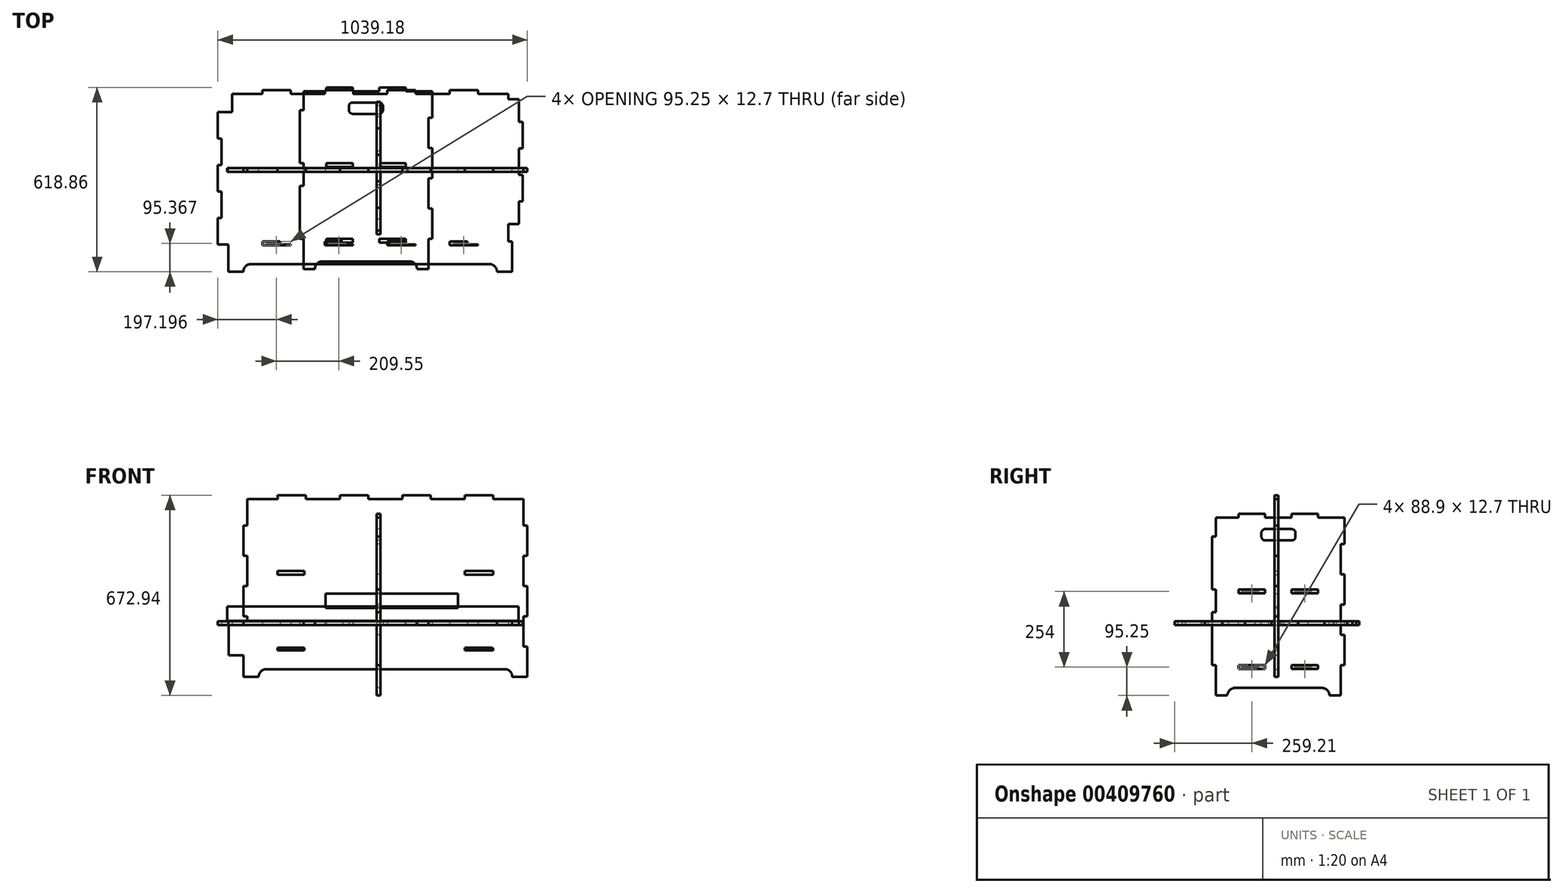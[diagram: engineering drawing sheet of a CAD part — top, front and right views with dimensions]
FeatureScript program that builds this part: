
annotation { "Feature Type Name" : "Feature", "Feature Type Description" : "" }
export const myFeature = defineFeature(function(context is Context, id is Id, definition is map)
    precondition{}
    {
        {
            var Q0;
            Q0=qCreatedBy(makeId("Top.planeOp"),FACE);
            var sketch = newSketch(context, id + "F0", { "sketchPlane" : qUnion([Q0])});
            skLineSegment(sketch, "E0.bottom", {"start": v(-520.7, -256.61) * mm, "end": v(-419.1, -256.61) * mm});
            skLineSegment(sketch, "E0.top", {"start": v(-520.7, 187.89) * mm, "end": v(-419.1, 187.89) * mm});
            skLineSegment(sketch, "E0.left", {"start": v(-520.7, -167.71) * mm, "end": v(-520.7, -78.8) * mm});
            skLineSegment(sketch, "E0.right", {"start": v(406.4, -167.71) * mm, "end": v(406.4, -79.99) * mm});
            skLineSegment(sketch, "E1.bottom", {"start": v(-533.4, 187.9) * mm, "end": v(-520.7, 187.9) * mm});
            skLineSegment(sketch, "E1.top", {"start": v(-533.4, 99) * mm, "end": v(-520.7, 99) * mm});
            skLineSegment(sketch, "E1.left", {"start": v(-533.4, 187.9) * mm, "end": v(-533.4, 99) * mm});
            skLineSegment(sketch, "E1.right", {"start": v(-520.7, 187.9) * mm, "end": v(-520.7, 187.89) * mm});
            skLineSegment(sketch, "E2.bottom", {"start": v(-520.7, -256.61) * mm, "end": v(-533.4, -256.61) * mm});
            skLineSegment(sketch, "E2.top", {"start": v(-520.7, -167.71) * mm, "end": v(-533.4, -167.71) * mm});
            skLineSegment(sketch, "E2.right", {"start": v(-533.4, -256.61) * mm, "end": v(-533.4, -167.71) * mm});
            skLineSegment(sketch, "E3.bottom", {"start": v(-533.4, 10.1) * mm, "end": v(-520.7, 10.1) * mm});
            skLineSegment(sketch, "E3.top", {"start": v(-533.4, -78.8) * mm, "end": v(-520.7, -78.8) * mm});
            skLineSegment(sketch, "E3.left", {"start": v(-533.4, 10.1) * mm, "end": v(-533.4, -78.8) * mm});
            skLineSegment(sketch, "E4.top", {"start": v(406.4, 98.99) * mm, "end": v(419.1, 98.99) * mm});
            skLineSegment(sketch, "E5.top", {"start": v(406.4, -167.71) * mm, "end": v(419.1, -167.71) * mm});
            skLineSegment(sketch, "E6.bottom", {"start": v(406.4, 10.09) * mm, "end": v(419.1, 10.09) * mm});
            skLineSegment(sketch, "E6.top", {"start": v(406.4, -79.99) * mm, "end": v(419.1, -79.99) * mm});
            skLineSegment(sketch, "E6.right", {"start": v(419.1, 10.09) * mm, "end": v(419.1, -79.99) * mm});
            skLineSegment(sketch, "E7.top", {"start": v(-419.1, 175.19) * mm, "end": v(-323.85, 175.19) * mm});
            skLineSegment(sketch, "E7.left", {"start": v(-419.1, 187.89) * mm, "end": v(-419.1, 175.19) * mm});
            skLineSegment(sketch, "E7.right", {"start": v(-323.85, 187.89) * mm, "end": v(-323.85, 175.19) * mm});
            skLineSegment(sketch, "E8.trimOffspring", {"start": v(-323.85, 187.89) * mm, "end": v(-209.55, 187.89) * mm});
            skLineSegment(sketch, "E9.trimOffspring", {"start": v(-520.7, 10.1) * mm, "end": v(-520.7, 99) * mm});
            skLineSegment(sketch, "E10.trimOffspring", {"start": v(406.4, 10.09) * mm, "end": v(406.4, 98.99) * mm});
            skLineSegment(sketch, "E11.top", {"start": v(-209.55, 175.19) * mm, "end": v(-114.3, 175.19) * mm});
            skLineSegment(sketch, "E11.left", {"start": v(-209.55, 187.89) * mm, "end": v(-209.55, 175.19) * mm});
            skLineSegment(sketch, "E11.right", {"start": v(-114.3, 187.89) * mm, "end": v(-114.3, 175.19) * mm});
            skLineSegment(sketch, "E12.top", {"start": v(0, 175.19) * mm, "end": v(95.25, 175.19) * mm});
            skLineSegment(sketch, "E12.left", {"start": v(0, 187.89) * mm, "end": v(0, 175.19) * mm});
            skLineSegment(sketch, "E12.right", {"start": v(95.25, 187.89) * mm, "end": v(95.25, 175.19) * mm});
            skLineSegment(sketch, "E13.top", {"start": v(209.55, 175.19) * mm, "end": v(304.8, 175.19) * mm});
            skLineSegment(sketch, "E13.left", {"start": v(209.55, 187.89) * mm, "end": v(209.55, 175.19) * mm});
            skLineSegment(sketch, "E13.right", {"start": v(304.8, 187.89) * mm, "end": v(304.8, 175.19) * mm});
            skLineSegment(sketch, "E14.trimOffspring", {"start": v(-114.3, 187.89) * mm, "end": v(0, 187.89) * mm});
            skLineSegment(sketch, "E15.trimOffspring", {"start": v(95.25, 187.89) * mm, "end": v(209.55, 187.89) * mm});
            skLineSegment(sketch, "E16.top", {"start": v(-419.1, -243.91) * mm, "end": v(-323.85, -243.91) * mm});
            skLineSegment(sketch, "E16.left", {"start": v(-419.1, -256.61) * mm, "end": v(-419.1, -243.91) * mm});
            skLineSegment(sketch, "E16.right", {"start": v(-323.85, -256.61) * mm, "end": v(-323.85, -243.91) * mm});
            skLineSegment(sketch, "E17.top", {"start": v(-209.55, -243.91) * mm, "end": v(-114.3, -243.91) * mm});
            skLineSegment(sketch, "E17.left", {"start": v(-209.55, -256.61) * mm, "end": v(-209.55, -243.91) * mm});
            skLineSegment(sketch, "E17.right", {"start": v(-114.3, -256.61) * mm, "end": v(-114.3, -243.91) * mm});
            skLineSegment(sketch, "E18.top", {"start": v(0, -243.91) * mm, "end": v(95.25, -243.91) * mm});
            skLineSegment(sketch, "E18.left", {"start": v(0, -256.61) * mm, "end": v(0, -243.91) * mm});
            skLineSegment(sketch, "E18.right", {"start": v(95.25, -256.61) * mm, "end": v(95.25, -243.91) * mm});
            skLineSegment(sketch, "E19.top", {"start": v(209.55, -243.91) * mm, "end": v(304.8, -243.91) * mm});
            skLineSegment(sketch, "E19.left", {"start": v(209.55, -256.61) * mm, "end": v(209.55, -243.91) * mm});
            skLineSegment(sketch, "E19.right", {"start": v(304.8, -256.61) * mm, "end": v(304.8, -243.91) * mm});
            skLineSegment(sketch, "E20.trimOffspring", {"start": v(-323.85, -256.61) * mm, "end": v(-209.55, -256.61) * mm});
            skLineSegment(sketch, "E21.trimOffspring", {"start": v(-114.3, -256.61) * mm, "end": v(0, -256.61) * mm});
            skLineSegment(sketch, "E22.trimOffspring", {"start": v(95.25, -256.61) * mm, "end": v(209.55, -256.61) * mm});
            skLineSegment(sketch, "E23.trimOffspring", {"start": v(304.8, -256.61) * mm, "end": v(406.4, -256.61) * mm});
            skPoint(sketch, "E24.right.end.orphan", {"position": v(419.1, 175.19) * mm});
            skPoint(sketch, "E4.right.start.orphan", {"position": v(433.58, 187.89) * mm});
            skLineSegment(sketch, "E25", {"start": v(419.1, 98.99) * mm, "end": v(419.1, 187.89) * mm});
            skPoint(sketch, "E4.bottom.start.orphan", {"position": v(406.4, 187.89) * mm});
            skLineSegment(sketch, "E26", {"start": v(304.8, 187.89) * mm, "end": v(419.1, 187.89) * mm});
            skLineSegment(sketch, "E27", {"start": v(419.1, -167.71) * mm, "end": v(419.1, -256.61) * mm});
            skLineSegment(sketch, "E28", {"start": v(419.1, -256.61) * mm, "end": v(406.4, -256.61) * mm});
            skSolve(sketch);
        }
        {
            var Q0;
            Q0 = qSketchRegion(id + "F0", true);
            extrude(context, id + "F1", {"entities" : qUnion([Q0]), "depth" : 12.7 * mm});
        }
        {
            var Q0;
            Q0=qCreatedBy(makeId("Top.planeOp"),FACE);
            var sketch = newSketch(context, id + "F2", { "sketchPlane" : qUnion([Q0])});
            skLineSegment(sketch, "E29.bottom", {"start": v(-347.77, 244.35) * mm, "end": v(-252.52, 244.35) * mm});
            skLineSegment(sketch, "E29.top", {"start": v(-347.77, -200.15) * mm, "end": v(-252.52, -200.15) * mm});
            skLineSegment(sketch, "E29.left", {"start": v(-449.37, 231.65) * mm, "end": v(-449.37, 155.45) * mm});
            skLineSegment(sketch, "E29.right", {"start": v(477.73, 231.65) * mm, "end": v(477.73, 155.45) * mm});
            skLineSegment(sketch, "E30.bottom", {"start": v(-449.37, 155.45) * mm, "end": v(-462.07, 155.45) * mm});
            skLineSegment(sketch, "E30.top", {"start": v(-449.37, 66.55) * mm, "end": v(-462.07, 66.55) * mm});
            skLineSegment(sketch, "E30.right", {"start": v(-462.07, 155.45) * mm, "end": v(-462.07, 66.55) * mm});
            skLineSegment(sketch, "E31.bottom", {"start": v(-449.37, -22.35) * mm, "end": v(-462.07, -22.35) * mm});
            skLineSegment(sketch, "E31.top", {"start": v(-449.37, -111.25) * mm, "end": v(-462.07, -111.25) * mm});
            skLineSegment(sketch, "E31.right", {"start": v(-462.07, -22.35) * mm, "end": v(-462.07, -111.25) * mm});
            skLineSegment(sketch, "E32.trimOffspring", {"start": v(-449.37, 66.55) * mm, "end": v(-449.37, -22.35) * mm});
            skLineSegment(sketch, "E33.trimOffspring", {"start": v(-449.37, -111.25) * mm, "end": v(-449.37, -187.45) * mm});
            skLineSegment(sketch, "E34.bottom", {"start": v(477.73, 155.45) * mm, "end": v(490.43, 155.45) * mm});
            skLineSegment(sketch, "E34.top", {"start": v(477.73, 66.55) * mm, "end": v(490.43, 66.55) * mm});
            skLineSegment(sketch, "E34.right", {"start": v(490.43, 155.45) * mm, "end": v(490.43, 66.55) * mm});
            skLineSegment(sketch, "E35.bottom", {"start": v(477.73, -22.35) * mm, "end": v(490.43, -22.35) * mm});
            skLineSegment(sketch, "E35.top", {"start": v(477.73, -111.25) * mm, "end": v(490.43, -111.25) * mm});
            skLineSegment(sketch, "E35.right", {"start": v(490.43, -22.35) * mm, "end": v(490.43, -111.25) * mm});
            skLineSegment(sketch, "E36.trimOffspring", {"start": v(477.73, 66.55) * mm, "end": v(477.73, -22.35) * mm});
            skLineSegment(sketch, "E37.trimOffspring", {"start": v(477.73, -111.25) * mm, "end": v(477.73, -187.45) * mm});
            skLineSegment(sketch, "E38.top", {"start": v(-449.37, 231.65) * mm, "end": v(-347.77, 231.65) * mm});
            skLineSegment(sketch, "E38.right", {"start": v(-347.77, 244.35) * mm, "end": v(-347.77, 231.65) * mm});
            skLineSegment(sketch, "E39.top", {"start": v(-252.52, 231.65) * mm, "end": v(-138.22, 231.65) * mm});
            skLineSegment(sketch, "E39.left", {"start": v(-252.52, 244.35) * mm, "end": v(-252.52, 231.65) * mm});
            skLineSegment(sketch, "E39.right", {"start": v(-138.22, 244.35) * mm, "end": v(-138.22, 231.65) * mm});
            skPoint(sketch, "E38.left.start.orphan", {"position": v(-449.37, 244.35) * mm});
            skPoint(sketch, "E40.trimOffspring.end.orphan", {"position": v(14.18, 244.35) * mm});
            skLineSegment(sketch, "E41", {"start": v(-138.22, 244.35) * mm, "end": v(-42.97, 244.35) * mm});
            skLineSegment(sketch, "E42.top", {"start": v(-42.97, 231.65) * mm, "end": v(71.33, 231.65) * mm});
            skLineSegment(sketch, "E42.left", {"start": v(-42.97, 244.35) * mm, "end": v(-42.97, 231.65) * mm});
            skLineSegment(sketch, "E42.right", {"start": v(71.33, 244.35) * mm, "end": v(71.33, 231.65) * mm});
            skLineSegment(sketch, "E43.trimOffspring", {"start": v(71.33, 244.35) * mm, "end": v(166.58, 244.35) * mm});
            skLineSegment(sketch, "E44.top", {"start": v(166.58, 231.65) * mm, "end": v(280.88, 231.65) * mm});
            skLineSegment(sketch, "E44.left", {"start": v(166.58, 244.35) * mm, "end": v(166.58, 231.65) * mm});
            skLineSegment(sketch, "E44.right", {"start": v(280.88, 244.35) * mm, "end": v(280.88, 231.65) * mm});
            skLineSegment(sketch, "E45.trimOffspring", {"start": v(280.88, 244.35) * mm, "end": v(376.13, 244.35) * mm});
            skLineSegment(sketch, "E46.top", {"start": v(477.73, 231.65) * mm, "end": v(376.13, 231.65) * mm});
            skLineSegment(sketch, "E46.right", {"start": v(376.13, 244.35) * mm, "end": v(376.13, 231.65) * mm});
            skPoint(sketch, "E47.orphan", {"position": v(477.73, 244.35) * mm});
            skLineSegment(sketch, "E48.top", {"start": v(-347.77, -187.45) * mm, "end": v(-449.37, -187.45) * mm});
            skLineSegment(sketch, "E48.left", {"start": v(-347.77, -200.15) * mm, "end": v(-347.77, -187.45) * mm});
            skLineSegment(sketch, "E49.top", {"start": v(-252.52, -187.45) * mm, "end": v(-138.22, -187.45) * mm});
            skLineSegment(sketch, "E49.left", {"start": v(-252.52, -200.15) * mm, "end": v(-252.52, -187.45) * mm});
            skLineSegment(sketch, "E49.right", {"start": v(-138.22, -200.15) * mm, "end": v(-138.22, -187.45) * mm});
            skLineSegment(sketch, "E50.top", {"start": v(-42.97, -187.45) * mm, "end": v(71.33, -187.45) * mm});
            skLineSegment(sketch, "E50.left", {"start": v(-42.97, -200.15) * mm, "end": v(-42.97, -187.45) * mm});
            skLineSegment(sketch, "E50.right", {"start": v(71.33, -200.15) * mm, "end": v(71.33, -187.45) * mm});
            skLineSegment(sketch, "E51.top", {"start": v(166.58, -187.45) * mm, "end": v(280.88, -187.45) * mm});
            skLineSegment(sketch, "E51.left", {"start": v(166.58, -200.15) * mm, "end": v(166.58, -187.45) * mm});
            skLineSegment(sketch, "E51.right", {"start": v(280.88, -200.15) * mm, "end": v(280.88, -187.45) * mm});
            skLineSegment(sketch, "E52.top", {"start": v(376.13, -187.45) * mm, "end": v(477.73, -187.45) * mm});
            skLineSegment(sketch, "E52.left", {"start": v(376.13, -200.15) * mm, "end": v(376.13, -187.45) * mm});
            skPoint(sketch, "E48.right.start.orphan", {"position": v(-449.37, -200.15) * mm});
            skLineSegment(sketch, "E53.trimOffspring", {"start": v(-138.22, -200.15) * mm, "end": v(-42.97, -200.15) * mm});
            skLineSegment(sketch, "E54.trimOffspring", {"start": v(71.33, -200.15) * mm, "end": v(166.58, -200.15) * mm});
            skLineSegment(sketch, "E55.trimOffspring", {"start": v(280.88, -200.15) * mm, "end": v(376.13, -200.15) * mm});
            skPoint(sketch, "E56.orphan", {"position": v(477.73, -200.15) * mm});
            skSolve(sketch);
        }
        {
            var Q0;
            Q0=makeQuery(id+"F2.imprint","IMPRINT",FACE,{"disambiguationData":[TD([[makeQuery(id+"F2.imprint","IMPRINT",EDGE,{"derivedFrom":sQuery(id+"F2.wireOp",EDGE,"E29.bottom")}),-1.0]])]});
            extrude(context, id + "F3", {"entities" : qUnion([Q0]), "depth" : 12.7 * mm});
        }
        {
            var Q0;
            Q0=qCreatedBy(makeId("Front.planeOp"),FACE);
            var sketch = newSketch(context, id + "F4", { "sketchPlane" : qUnion([Q0])});
            skLineSegment(sketch, "E57.bottom", {"start": v(-446.72, -173.54) * mm, "end": v(-395.92, -173.54) * mm});
            skLineSegment(sketch, "E57.top", {"start": v(-332.42, 436.06) * mm, "end": v(-237.17, 436.06) * mm});
            skLineSegment(sketch, "E57.left", {"start": v(-446.72, -173.54) * mm, "end": v(-446.72, -71.94) * mm});
            skLineSegment(sketch, "E57.right", {"start": v(505.78, -173.66) * mm, "end": v(505.78, -72.06) * mm});
            skLineSegment(sketch, "E58.top", {"start": v(-434.02, 423.36) * mm, "end": v(-331.85, 423.36) * mm});
            skLineSegment(sketch, "E58.right", {"start": v(-332.42, 436.06) * mm, "end": v(-331.85, 423.36) * mm});
            skLineSegment(sketch, "E59.top", {"start": v(-237.17, 423.24) * mm, "end": v(-122.87, 423.24) * mm});
            skLineSegment(sketch, "E59.left", {"start": v(-237.17, 436.06) * mm, "end": v(-237.17, 423.24) * mm});
            skLineSegment(sketch, "E59.right", {"start": v(-122.87, 436.06) * mm, "end": v(-122.87, 423.24) * mm});
            skLineSegment(sketch, "E60.top", {"start": v(-27.62, 423.24) * mm, "end": v(86.68, 423.24) * mm});
            skLineSegment(sketch, "E60.left", {"start": v(-27.62, 436.06) * mm, "end": v(-27.62, 423.24) * mm});
            skLineSegment(sketch, "E60.right", {"start": v(86.68, 436.06) * mm, "end": v(86.68, 423.24) * mm});
            skLineSegment(sketch, "E61.top", {"start": v(181.93, 423.24) * mm, "end": v(296.23, 423.24) * mm});
            skLineSegment(sketch, "E61.left", {"start": v(181.93, 436.06) * mm, "end": v(181.93, 423.24) * mm});
            skLineSegment(sketch, "E61.right", {"start": v(296.23, 436.06) * mm, "end": v(296.23, 423.24) * mm});
            skLineSegment(sketch, "E62.top", {"start": v(391.48, 423.36) * mm, "end": v(493.08, 423.36) * mm});
            skLineSegment(sketch, "E62.left", {"start": v(391.48, 436.06) * mm, "end": v(391.48, 423.36) * mm});
            skLineSegment(sketch, "E63.trimOffspring", {"start": v(-122.87, 436.06) * mm, "end": v(-27.62, 436.06) * mm});
            skLineSegment(sketch, "E64.trimOffspring", {"start": v(86.68, 436.06) * mm, "end": v(181.93, 436.06) * mm});
            skLineSegment(sketch, "E65.trimOffspring", {"start": v(296.23, 436.06) * mm, "end": v(391.48, 436.06) * mm});
            skLineSegment(sketch, "E66.top", {"start": v(-370.52, -148.14) * mm, "end": v(429.58, -148.14) * mm});
            skLineSegment(sketch, "E66.left", {"start": v(-395.92, -173.54) * mm, "end": v(-395.92, -173.54) * mm});
            skPoint(sketch, "E67.visualSharp", {"position": v(-395.92, -148.14) * mm});
            skArc(sketch, "E67.filletArc", {"start": v(-370.52, -148.14) * mm, "mid": v(-388.48, -155.58) * mm, "end": v(-395.92, -173.54) * mm});
            skPoint(sketch, "E68.visualSharp", {"position": v(454.98, -148.14) * mm});
            skArc(sketch, "E68.filletArc", {"start": v(454.98, -173.66) * mm, "mid": v(447.58, -155.62) * mm, "end": v(429.58, -148.14) * mm});
            skLineSegment(sketch, "E69.trimOffspring", {"start": v(454.98, -173.66) * mm, "end": v(505.78, -173.66) * mm});
            skLineSegment(sketch, "E70.top", {"start": v(505.78, 334.34) * mm, "end": v(493.08, 334.34) * mm});
            skLineSegment(sketch, "E70.right", {"start": v(493.08, 423.36) * mm, "end": v(493.08, 334.34) * mm});
            skLineSegment(sketch, "E71.bottom", {"start": v(505.78, 232.74) * mm, "end": v(493.08, 232.74) * mm});
            skLineSegment(sketch, "E71.top", {"start": v(505.78, 131.14) * mm, "end": v(493.08, 131.14) * mm});
            skLineSegment(sketch, "E71.right", {"start": v(493.08, 232.74) * mm, "end": v(493.08, 131.14) * mm});
            skLineSegment(sketch, "E72.bottom", {"start": v(505.78, 29.54) * mm, "end": v(493.08, 29.54) * mm});
            skLineSegment(sketch, "E72.top", {"start": v(505.78, -72.06) * mm, "end": v(493.08, -72.06) * mm});
            skLineSegment(sketch, "E72.right", {"start": v(493.08, 29.54) * mm, "end": v(493.08, -72.06) * mm});
            skLineSegment(sketch, "E73.top", {"start": v(-446.72, 334.46) * mm, "end": v(-434.02, 334.46) * mm});
            skLineSegment(sketch, "E73.right", {"start": v(-434.02, 423.36) * mm, "end": v(-434.02, 334.46) * mm});
            skPoint(sketch, "E74.oppositeSnap0", {"position": v(-446.72, 131.26) * mm});
            skLineSegment(sketch, "E74.bottom", {"start": v(-446.72, 232.86) * mm, "end": v(-434.02, 232.86) * mm});
            skLineSegment(sketch, "E74.top", {"start": v(-446.72, 131.26) * mm, "end": v(-434.02, 131.26) * mm});
            skLineSegment(sketch, "E74.right", {"start": v(-434.02, 232.86) * mm, "end": v(-434.02, 131.26) * mm});
            skLineSegment(sketch, "E75.bottom", {"start": v(-446.72, 29.66) * mm, "end": v(-434.02, 29.66) * mm});
            skLineSegment(sketch, "E75.top", {"start": v(-446.72, -71.94) * mm, "end": v(-434.02, -71.94) * mm});
            skLineSegment(sketch, "E75.right", {"start": v(-434.02, 29.66) * mm, "end": v(-434.02, -71.94) * mm});
            skPoint(sketch, "E76.trimOffspring.start.orphan", {"position": v(493.08, 435.94) * mm});
            skPoint(sketch, "E62.right.start.orphan", {"position": v(505.78, 435.94) * mm});
            skLineSegment(sketch, "E77.trimOffspring", {"start": v(505.78, 232.74) * mm, "end": v(505.78, 334.34) * mm});
            skLineSegment(sketch, "E78.trimOffspring", {"start": v(505.78, 29.54) * mm, "end": v(505.78, 131.14) * mm});
            skLineSegment(sketch, "E79.trimOffspring", {"start": v(-446.72, 232.86) * mm, "end": v(-446.72, 334.46) * mm});
            skLineSegment(sketch, "E80.trimOffspring", {"start": v(-446.72, 29.66) * mm, "end": v(-446.72, 131.26) * mm});
            skPoint(sketch, "E81.orphan", {"position": v(-446.72, 436.06) * mm});
            skPoint(sketch, "E82.orphan", {"position": v(-434.02, 436.06) * mm});
            skPoint(sketch, "E83.orphan", {"position": v(-446.72, 423.36) * mm});
            skLineSegment(sketch, "E84.bottom", {"start": v(-332.42, 182.06) * mm, "end": v(-237.17, 182.06) * mm});
            skLineSegment(sketch, "E84.top", {"start": v(-332.42, 169.36) * mm, "end": v(-237.17, 169.36) * mm});
            skLineSegment(sketch, "E84.left", {"start": v(-332.42, 182.06) * mm, "end": v(-332.42, 169.36) * mm});
            skLineSegment(sketch, "E84.right", {"start": v(-237.17, 182.06) * mm, "end": v(-237.17, 169.36) * mm});
            skLineSegment(sketch, "E85.bottom", {"start": v(-122.87, 182.06) * mm, "end": v(-27.62, 182.06) * mm});
            skLineSegment(sketch, "E85.top", {"start": v(-122.87, 169.74) * mm, "end": v(-27.62, 169.74) * mm});
            skLineSegment(sketch, "E85.left", {"start": v(-122.87, 182.06) * mm, "end": v(-122.87, 169.74) * mm});
            skLineSegment(sketch, "E85.right", {"start": v(-27.62, 182.06) * mm, "end": v(-27.62, 169.74) * mm});
            skLineSegment(sketch, "E86.bottom", {"start": v(86.68, 182.06) * mm, "end": v(181.93, 182.06) * mm});
            skLineSegment(sketch, "E86.top", {"start": v(86.68, 169.36) * mm, "end": v(181.93, 169.36) * mm});
            skLineSegment(sketch, "E86.left", {"start": v(86.68, 182.06) * mm, "end": v(86.68, 169.36) * mm});
            skLineSegment(sketch, "E86.right", {"start": v(181.93, 182.06) * mm, "end": v(181.93, 169.36) * mm});
            skLineSegment(sketch, "E87.bottom", {"start": v(296.23, 182.06) * mm, "end": v(391.48, 182.06) * mm});
            skLineSegment(sketch, "E87.top", {"start": v(296.23, 169.36) * mm, "end": v(391.48, 169.36) * mm});
            skLineSegment(sketch, "E87.left", {"start": v(296.23, 182.06) * mm, "end": v(296.23, 169.36) * mm});
            skLineSegment(sketch, "E87.right", {"start": v(391.48, 182.06) * mm, "end": v(391.48, 169.36) * mm});
            skLineSegment(sketch, "E88.bottom", {"start": v(-332.42, -71.94) * mm, "end": v(-237.17, -71.94) * mm});
            skLineSegment(sketch, "E88.top", {"start": v(-332.42, -84.64) * mm, "end": v(-237.17, -84.64) * mm});
            skLineSegment(sketch, "E88.left", {"start": v(-332.42, -71.94) * mm, "end": v(-332.42, -84.64) * mm});
            skLineSegment(sketch, "E88.right", {"start": v(-237.17, -71.94) * mm, "end": v(-237.17, -84.64) * mm});
            skLineSegment(sketch, "E89.bottom", {"start": v(-122.87, -71.94) * mm, "end": v(-27.62, -71.94) * mm});
            skLineSegment(sketch, "E89.top", {"start": v(-122.87, -84.64) * mm, "end": v(-27.62, -84.64) * mm});
            skLineSegment(sketch, "E89.left", {"start": v(-122.87, -71.94) * mm, "end": v(-122.87, -84.64) * mm});
            skLineSegment(sketch, "E89.right", {"start": v(-27.62, -71.94) * mm, "end": v(-27.62, -84.64) * mm});
            skPoint(sketch, "E90.oppositeSnap0", {"position": v(-75.24, -84.64) * mm});
            skLineSegment(sketch, "E90.bottom", {"start": v(86.68, -71.94) * mm, "end": v(181.93, -71.94) * mm});
            skLineSegment(sketch, "E90.top", {"start": v(86.68, -84.64) * mm, "end": v(181.93, -84.64) * mm});
            skLineSegment(sketch, "E90.left", {"start": v(86.68, -71.94) * mm, "end": v(86.68, -84.64) * mm});
            skLineSegment(sketch, "E90.right", {"start": v(181.93, -71.94) * mm, "end": v(181.93, -84.64) * mm});
            skLineSegment(sketch, "E91.bottom", {"start": v(296.23, -71.94) * mm, "end": v(391.48, -71.94) * mm});
            skLineSegment(sketch, "E91.top", {"start": v(296.23, -84.64) * mm, "end": v(391.48, -84.64) * mm});
            skLineSegment(sketch, "E91.left", {"start": v(296.23, -71.94) * mm, "end": v(296.23, -84.64) * mm});
            skLineSegment(sketch, "E91.right", {"start": v(391.48, -71.94) * mm, "end": v(391.48, -84.64) * mm});
            skPoint(sketch, "E66.right.start.orphan", {"position": v(454.98, -160.96) * mm});
            skSolve(sketch);
        }
        {
            var Q0;
            Q0 = qSketchRegion(id + "F4", true);
            extrude(context, id + "F5", {"entities" : qUnion([Q0]), "depth" : 12.7 * mm});
        }
        {
            var Q0;
            Q0=qCreatedBy(makeId("Right.planeOp"),FACE);
            var sketch = newSketch(context, id + "F6", { "sketchPlane" : qUnion([Q0])});
            skLineSegment(sketch, "E92.bottom", {"start": v(-132.95, 372.72) * mm, "end": v(-44.05, 372.72) * mm});
            skLineSegment(sketch, "E92.top", {"start": v(-209.15, -236.88) * mm, "end": v(-171.05, -236.88) * mm});
            skLineSegment(sketch, "E92.left", {"start": v(-221.85, 296.52) * mm, "end": v(-221.85, 118.72) * mm});
            skLineSegment(sketch, "E93.top", {"start": v(-145.65, -211.48) * mm, "end": v(146.45, -211.48) * mm});
            skLineSegment(sketch, "E93.left", {"start": v(-171.05, -236.88) * mm, "end": v(-171.05, -236.88) * mm});
            skLineSegment(sketch, "E93.right", {"start": v(171.85, -236.88) * mm, "end": v(171.85, -236.88) * mm});
            skLineSegment(sketch, "E94.trimOffspring", {"start": v(171.85, -236.88) * mm, "end": v(209.95, -236.88) * mm});
            skPoint(sketch, "E95.visualSharp", {"position": v(-171.05, -211.48) * mm});
            skArc(sketch, "E95.filletArc", {"start": v(-145.65, -211.48) * mm, "mid": v(-163.61, -218.92) * mm, "end": v(-171.05, -236.88) * mm});
            skPoint(sketch, "E96.visualSharp", {"position": v(171.85, -211.48) * mm});
            skArc(sketch, "E96.filletArc", {"start": v(171.85, -236.88) * mm, "mid": v(164.41, -218.92) * mm, "end": v(146.45, -211.48) * mm});
            skLineSegment(sketch, "E97.top", {"start": v(-209.15, 360.02) * mm, "end": v(-132.95, 360.02) * mm});
            skLineSegment(sketch, "E97.right", {"start": v(-132.95, 372.72) * mm, "end": v(-132.95, 360.02) * mm});
            skLineSegment(sketch, "E98.top", {"start": v(-44.05, 360.02) * mm, "end": v(44.85, 360.02) * mm});
            skLineSegment(sketch, "E98.left", {"start": v(-44.05, 372.72) * mm, "end": v(-44.05, 360.02) * mm});
            skLineSegment(sketch, "E98.right", {"start": v(44.85, 372.72) * mm, "end": v(44.85, 360.02) * mm});
            skLineSegment(sketch, "E99.top", {"start": v(209.95, 360.02) * mm, "end": v(133.75, 360.02) * mm});
            skLineSegment(sketch, "E99.right", {"start": v(133.75, 372.72) * mm, "end": v(133.75, 360.02) * mm});
            skLineSegment(sketch, "E100.top", {"start": v(222.65, 271.12) * mm, "end": v(209.95, 271.12) * mm});
            skLineSegment(sketch, "E101.bottom", {"start": v(222.65, 169.52) * mm, "end": v(209.95, 169.52) * mm});
            skLineSegment(sketch, "E101.top", {"start": v(222.65, 67.92) * mm, "end": v(209.95, 67.92) * mm});
            skLineSegment(sketch, "E102.bottom", {"start": v(222.65, -33.68) * mm, "end": v(209.95, -33.68) * mm});
            skLineSegment(sketch, "E102.top", {"start": v(222.65, -135.28) * mm, "end": v(209.95, -135.28) * mm});
            skLineSegment(sketch, "E103.bottom", {"start": v(-132.95, 118.72) * mm, "end": v(-44.05, 118.72) * mm});
            skLineSegment(sketch, "E103.top", {"start": v(-132.95, 106.02) * mm, "end": v(-44.05, 106.02) * mm});
            skLineSegment(sketch, "E103.left", {"start": v(-132.95, 118.72) * mm, "end": v(-132.95, 106.02) * mm});
            skLineSegment(sketch, "E103.right", {"start": v(-44.05, 118.72) * mm, "end": v(-44.05, 106.02) * mm});
            skLineSegment(sketch, "E104.bottom", {"start": v(44.85, 118.72) * mm, "end": v(133.75, 118.72) * mm});
            skLineSegment(sketch, "E104.top", {"start": v(44.85, 106.02) * mm, "end": v(133.75, 106.02) * mm});
            skLineSegment(sketch, "E104.left", {"start": v(44.85, 118.72) * mm, "end": v(44.85, 106.02) * mm});
            skLineSegment(sketch, "E104.right", {"start": v(133.75, 118.72) * mm, "end": v(133.75, 106.02) * mm});
            skLineSegment(sketch, "E105.bottom", {"start": v(-132.95, -135.28) * mm, "end": v(-44.05, -135.28) * mm});
            skLineSegment(sketch, "E105.top", {"start": v(-132.95, -147.98) * mm, "end": v(-44.05, -147.98) * mm});
            skLineSegment(sketch, "E105.left", {"start": v(-132.95, -135.28) * mm, "end": v(-132.95, -147.98) * mm});
            skLineSegment(sketch, "E105.right", {"start": v(-44.05, -135.28) * mm, "end": v(-44.05, -147.98) * mm});
            skLineSegment(sketch, "E106.bottom", {"start": v(44.85, -135.28) * mm, "end": v(133.75, -135.28) * mm});
            skLineSegment(sketch, "E106.top", {"start": v(44.85, -147.98) * mm, "end": v(133.75, -147.98) * mm});
            skLineSegment(sketch, "E106.left", {"start": v(44.85, -135.28) * mm, "end": v(44.85, -147.98) * mm});
            skLineSegment(sketch, "E106.right", {"start": v(133.75, -135.28) * mm, "end": v(133.75, -147.98) * mm});
            skLineSegment(sketch, "E107.bottom", {"start": v(-44.05, 321.92) * mm, "end": v(44.85, 321.92) * mm});
            skLineSegment(sketch, "E107.top", {"start": v(-44.05, 283.82) * mm, "end": v(44.85, 283.82) * mm});
            skLineSegment(sketch, "E107.left", {"start": v(-56.75, 309.22) * mm, "end": v(-56.75, 296.52) * mm});
            skLineSegment(sketch, "E107.right", {"start": v(57.55, 309.22) * mm, "end": v(57.55, 296.52) * mm});
            skLineSegment(sketch, "E108.top", {"start": v(-221.85, 296.52) * mm, "end": v(-209.15, 296.52) * mm});
            skLineSegment(sketch, "E108.right", {"start": v(-209.15, 360.02) * mm, "end": v(-209.15, 296.52) * mm});
            skLineSegment(sketch, "E109.bottom", {"start": v(-221.85, 118.72) * mm, "end": v(-209.15, 118.72) * mm});
            skLineSegment(sketch, "E109.top", {"start": v(-221.85, 42.52) * mm, "end": v(-209.15, 42.52) * mm});
            skLineSegment(sketch, "E109.right", {"start": v(-209.15, 118.72) * mm, "end": v(-209.15, 42.52) * mm});
            skLineSegment(sketch, "E110.top", {"start": v(-221.85, -135.28) * mm, "end": v(-209.15, -135.28) * mm});
            skLineSegment(sketch, "E110.right", {"start": v(-209.15, -236.88) * mm, "end": v(-209.15, -135.28) * mm});
            skPoint(sketch, "E108.bottom.start.orphan", {"position": v(-221.85, 372.72) * mm});
            skPoint(sketch, "E111.orphan", {"position": v(-209.15, 372.72) * mm});
            skLineSegment(sketch, "E112.trimOffspring", {"start": v(44.85, 372.72) * mm, "end": v(133.75, 372.72) * mm});
            skPoint(sketch, "E113.trimOffspring.end.orphan", {"position": v(222.65, 372.72) * mm});
            skPoint(sketch, "E114.orphan", {"position": v(222.65, 360.02) * mm});
            skPoint(sketch, "E115.orphan", {"position": v(209.95, 372.72) * mm});
            skLineSegment(sketch, "E116.trimOffspring", {"start": v(-221.85, 42.52) * mm, "end": v(-221.85, -135.28) * mm});
            skPoint(sketch, "E117.orphan", {"position": v(-221.85, -236.88) * mm});
            skPoint(sketch, "E118.visualSharp", {"position": v(57.55, 321.92) * mm});
            skArc(sketch, "E118.filletArc", {"start": v(57.55, 309.22) * mm, "mid": v(53.83, 318.2) * mm, "end": v(44.85, 321.92) * mm});
            skPoint(sketch, "E119.visualSharp", {"position": v(57.55, 283.82) * mm});
            skArc(sketch, "E119.filletArc", {"start": v(44.85, 283.82) * mm, "mid": v(53.83, 287.54) * mm, "end": v(57.55, 296.52) * mm});
            skPoint(sketch, "E120.visualSharp", {"position": v(-56.75, 283.82) * mm});
            skArc(sketch, "E120.filletArc", {"start": v(-56.75, 296.52) * mm, "mid": v(-53.03, 287.54) * mm, "end": v(-44.05, 283.82) * mm});
            skPoint(sketch, "E121.visualSharp", {"position": v(-56.75, 321.92) * mm});
            skArc(sketch, "E121.filletArc", {"start": v(-44.05, 321.92) * mm, "mid": v(-53.03, 318.2) * mm, "end": v(-56.75, 309.22) * mm});
            skLineSegment(sketch, "E122.bottom", {"start": v(209.95, 360.02) * mm, "end": v(222.65, 360.02) * mm});
            skLineSegment(sketch, "E122.top", {"start": v(209.95, 271.12) * mm, "end": v(222.65, 271.12) * mm});
            skLineSegment(sketch, "E122.right", {"start": v(222.65, 360.02) * mm, "end": v(222.65, 271.12) * mm});
            skLineSegment(sketch, "E123.bottom", {"start": v(209.95, 169.52) * mm, "end": v(222.65, 169.52) * mm});
            skLineSegment(sketch, "E123.top", {"start": v(209.95, 67.92) * mm, "end": v(222.65, 67.92) * mm});
            skLineSegment(sketch, "E123.right", {"start": v(222.65, 169.52) * mm, "end": v(222.65, 67.92) * mm});
            skLineSegment(sketch, "E124.bottom", {"start": v(209.95, -33.68) * mm, "end": v(222.65, -33.68) * mm});
            skLineSegment(sketch, "E124.top", {"start": v(209.95, -135.28) * mm, "end": v(222.65, -135.28) * mm});
            skLineSegment(sketch, "E124.right", {"start": v(222.65, -33.68) * mm, "end": v(222.65, -135.28) * mm});
            skLineSegment(sketch, "E125.left", {"start": v(209.95, 271.12) * mm, "end": v(209.95, 169.52) * mm});
            skLineSegment(sketch, "E126.left", {"start": v(209.95, 67.92) * mm, "end": v(209.95, -33.68) * mm});
            skLineSegment(sketch, "E127.left", {"start": v(209.95, -135.28) * mm, "end": v(209.95, -236.88) * mm});
            skPoint(sketch, "E127.top.end.orphan", {"position": v(222.65, -236.88) * mm});
            skSolve(sketch);
        }
        {
            var Q0;
            Q0 = qSketchRegion(id + "F6", true);
            extrude(context, id + "F7", {"entities" : qUnion([Q0]), "depth" : 12.7 * mm});
        }
        {
            var Q0;
            Q0=qCreatedBy(makeId("Front.planeOp"),FACE);
            var sketch = newSketch(context, id + "F8", { "sketchPlane" : qUnion([Q0])});
            skLineSegment(sketch, "E128.bottom", {"start": v(-361.95, 0) * mm, "end": v(-266.7, 0) * mm});
            skLineSegment(sketch, "E128.top", {"start": v(-476.25, -76.2) * mm, "end": v(476.25, -76.2) * mm});
            skLineSegment(sketch, "E128.left", {"start": v(-476.25, -12.7) * mm, "end": v(-476.25, -76.2) * mm});
            skLineSegment(sketch, "E128.right", {"start": v(476.25, -12.7) * mm, "end": v(476.25, -76.2) * mm});
            skLineSegment(sketch, "E129.top", {"start": v(-476.25, -12.7) * mm, "end": v(-361.95, -12.7) * mm});
            skLineSegment(sketch, "E129.right", {"start": v(-361.95, 0) * mm, "end": v(-361.95, -12.7) * mm});
            skLineSegment(sketch, "E130.top", {"start": v(-266.7, -12.7) * mm, "end": v(-152.4, -12.7) * mm});
            skLineSegment(sketch, "E130.left", {"start": v(-266.7, 0) * mm, "end": v(-266.7, -12.7) * mm});
            skLineSegment(sketch, "E130.right", {"start": v(-152.4, 0) * mm, "end": v(-152.4, -12.7) * mm});
            skLineSegment(sketch, "E131.top", {"start": v(-57.15, -12.7) * mm, "end": v(57.15, -12.7) * mm});
            skLineSegment(sketch, "E131.left", {"start": v(-57.15, 0) * mm, "end": v(-57.15, -12.7) * mm});
            skLineSegment(sketch, "E131.right", {"start": v(57.15, 0) * mm, "end": v(57.15, -12.7) * mm});
            skLineSegment(sketch, "E132.top", {"start": v(152.4, -12.7) * mm, "end": v(266.7, -12.7) * mm});
            skLineSegment(sketch, "E132.left", {"start": v(152.4, 0) * mm, "end": v(152.4, -12.7) * mm});
            skLineSegment(sketch, "E132.right", {"start": v(266.7, 0) * mm, "end": v(266.7, -12.7) * mm});
            skLineSegment(sketch, "E133.top", {"start": v(476.25, -12.7) * mm, "end": v(361.95, -12.7) * mm});
            skLineSegment(sketch, "E133.right", {"start": v(361.95, 0) * mm, "end": v(361.95, -12.7) * mm});
            skLineSegment(sketch, "E134.trimOffspring", {"start": v(-152.4, 0) * mm, "end": v(-57.15, 0) * mm});
            skLineSegment(sketch, "E135.trimOffspring", {"start": v(57.15, 0) * mm, "end": v(152.4, 0) * mm});
            skLineSegment(sketch, "E136.trimOffspring", {"start": v(266.7, 0) * mm, "end": v(361.95, 0) * mm});
            skPoint(sketch, "E137.orphan", {"position": v(476.25, 0) * mm});
            skPoint(sketch, "E138.orphan", {"position": v(-476.25, 0) * mm});
            skSolve(sketch);
        }
        {
            var Q0;
            Q0 = qSketchRegion(id + "F8", true);
            extrude(context, id + "F9", {"entities" : qUnion([Q0]), "depth" : 12.7 * mm});
        }
        {
            var Q0;
            Q0=qCreatedBy(makeId("Front.planeOp"),FACE);
            var sketch = newSketch(context, id + "F10", { "sketchPlane" : qUnion([Q0])});
            skLineSegment(sketch, "E139.bottom", {"start": v(-485.13, 0) * mm, "end": v(-370.83, 0) * mm});
            skLineSegment(sketch, "E139.top", {"start": v(-485.13, -76.2) * mm, "end": v(467.37, -76.2) * mm});
            skLineSegment(sketch, "E139.left", {"start": v(-485.13, 0) * mm, "end": v(-485.13, -76.2) * mm});
            skLineSegment(sketch, "E139.right", {"start": v(467.37, 0) * mm, "end": v(467.37, -76.2) * mm});
            skLineSegment(sketch, "E140.top", {"start": v(-370.83, -12.7) * mm, "end": v(-275.58, -12.7) * mm});
            skLineSegment(sketch, "E140.left", {"start": v(-370.83, 0) * mm, "end": v(-370.83, -12.7) * mm});
            skLineSegment(sketch, "E140.right", {"start": v(-275.58, 0) * mm, "end": v(-275.58, -12.7) * mm});
            skLineSegment(sketch, "E141.top", {"start": v(-161.28, -12.7) * mm, "end": v(-66.03, -12.7) * mm});
            skLineSegment(sketch, "E141.left", {"start": v(-161.28, 0) * mm, "end": v(-161.28, -12.7) * mm});
            skLineSegment(sketch, "E141.right", {"start": v(-66.03, 0) * mm, "end": v(-66.03, -12.7) * mm});
            skLineSegment(sketch, "E142.top", {"start": v(48.27, -12.7) * mm, "end": v(143.52, -12.7) * mm});
            skLineSegment(sketch, "E142.left", {"start": v(48.27, 0) * mm, "end": v(48.27, -12.7) * mm});
            skLineSegment(sketch, "E142.right", {"start": v(143.52, 0) * mm, "end": v(143.52, -12.7) * mm});
            skLineSegment(sketch, "E143.top", {"start": v(257.82, -12.7) * mm, "end": v(353.07, -12.7) * mm});
            skLineSegment(sketch, "E143.left", {"start": v(257.82, 0) * mm, "end": v(257.82, -12.7) * mm});
            skLineSegment(sketch, "E143.right", {"start": v(353.07, 0) * mm, "end": v(353.07, -12.7) * mm});
            skLineSegment(sketch, "E144.trimOffspring", {"start": v(-275.58, 0) * mm, "end": v(-161.28, 0) * mm});
            skLineSegment(sketch, "E145.trimOffspring", {"start": v(-66.03, 0) * mm, "end": v(48.27, 0) * mm});
            skLineSegment(sketch, "E146.trimOffspring", {"start": v(143.52, 0) * mm, "end": v(257.82, 0) * mm});
            skLineSegment(sketch, "E147.trimOffspring", {"start": v(353.07, 0) * mm, "end": v(467.37, 0) * mm});
            skSolve(sketch);
        }
        {
            var Q0;
            Q0=makeQuery(id+"F10.imprint","IMPRINT",FACE,{"disambiguationData":[TD([[makeQuery(id+"F10.imprint","IMPRINT",EDGE,{"derivedFrom":sQuery(id+"F10.wireOp",EDGE,"E139.bottom")}),-1.0]])]});
            var Q1;
            Q1 = qSketchRegion(id + "F10", true);
            extrude(context, id + "F11", {"entities" : qUnion([Q0, Q1]), "depth" : 12.7 * mm});
        }
        {
            var Q0;
            Q0=qCreatedBy(makeId("Front.planeOp"),FACE);
            var sketch = newSketch(context, id + "F12", { "sketchPlane" : qUnion([Q0])});
            skLineSegment(sketch, "E148.bottom", {"start": v(-496.15, 0) * mm, "end": v(-381.85, 0) * mm});
            skLineSegment(sketch, "E148.top", {"start": v(-496.15, -101.6) * mm, "end": v(-445.35, -101.6) * mm});
            skLineSegment(sketch, "E148.left", {"start": v(-496.15, 0) * mm, "end": v(-496.15, -101.6) * mm});
            skLineSegment(sketch, "E148.right", {"start": v(456.35, 0) * mm, "end": v(456.35, -101.6) * mm});
            skLineSegment(sketch, "E149.top", {"start": v(-419.95, -76.2) * mm, "end": v(380.15, -76.2) * mm});
            skLineSegment(sketch, "E149.left", {"start": v(-445.35, -101.6) * mm, "end": v(-445.35, -101.6) * mm});
            skLineSegment(sketch, "E149.right", {"start": v(405.55, -101.6) * mm, "end": v(405.55, -101.6) * mm});
            skLineSegment(sketch, "E150.trimOffspring", {"start": v(405.55, -101.6) * mm, "end": v(456.35, -101.6) * mm});
            skPoint(sketch, "E151.visualSharp", {"position": v(-445.35, -76.2) * mm});
            skArc(sketch, "E151.filletArc", {"start": v(-419.95, -76.2) * mm, "mid": v(-437.91, -83.64) * mm, "end": v(-445.35, -101.6) * mm});
            skPoint(sketch, "E152.visualSharp", {"position": v(405.55, -76.2) * mm});
            skArc(sketch, "E152.filletArc", {"start": v(405.55, -101.6) * mm, "mid": v(398.1, -83.64) * mm, "end": v(380.15, -76.2) * mm});
            skLineSegment(sketch, "E153.top", {"start": v(-381.85, -12.7) * mm, "end": v(-286.6, -12.7) * mm});
            skLineSegment(sketch, "E153.left", {"start": v(-381.85, 0) * mm, "end": v(-381.85, -12.7) * mm});
            skLineSegment(sketch, "E153.right", {"start": v(-286.6, 0) * mm, "end": v(-286.6, -12.7) * mm});
            skLineSegment(sketch, "E154.top", {"start": v(-172.3, -12.7) * mm, "end": v(-77.05, -12.7) * mm});
            skLineSegment(sketch, "E154.left", {"start": v(-172.3, 0) * mm, "end": v(-172.3, -12.7) * mm});
            skLineSegment(sketch, "E154.right", {"start": v(-77.05, 0) * mm, "end": v(-77.05, -12.7) * mm});
            skLineSegment(sketch, "E155.top", {"start": v(37.25, -12.7) * mm, "end": v(132.5, -12.7) * mm});
            skLineSegment(sketch, "E155.left", {"start": v(37.25, 0) * mm, "end": v(37.25, -12.7) * mm});
            skLineSegment(sketch, "E155.right", {"start": v(132.5, 0) * mm, "end": v(132.5, -12.7) * mm});
            skLineSegment(sketch, "E156.top", {"start": v(246.8, -12.7) * mm, "end": v(342.05, -12.7) * mm});
            skLineSegment(sketch, "E156.left", {"start": v(246.8, 0) * mm, "end": v(246.8, -12.7) * mm});
            skLineSegment(sketch, "E156.right", {"start": v(342.05, 0) * mm, "end": v(342.05, -12.7) * mm});
            skLineSegment(sketch, "E157.trimOffspring", {"start": v(-286.6, 0) * mm, "end": v(-172.3, 0) * mm});
            skLineSegment(sketch, "E158.trimOffspring", {"start": v(-77.05, 0) * mm, "end": v(37.25, 0) * mm});
            skLineSegment(sketch, "E159.trimOffspring", {"start": v(132.5, 0) * mm, "end": v(246.8, 0) * mm});
            skLineSegment(sketch, "E160.trimOffspring", {"start": v(342.05, 0) * mm, "end": v(456.35, 0) * mm});
            skSolve(sketch);
        }
        {
            var Q0;
            Q0 = qSketchRegion(id + "F12", true);
            extrude(context, id + "F13", {"entities" : qUnion([Q0]), "depth" : 12.7 * mm});
        }
        {
            var Q0;
            Q0=qCreatedBy(makeId("Top.planeOp"),FACE);
            var sketch = newSketch(context, id + "F14", { "sketchPlane" : qUnion([Q0])});
            skLineSegment(sketch, "E161.bottom", {"start": v(-169.48, 271.15) * mm, "end": v(-80.58, 271.15) * mm});
            skLineSegment(sketch, "E161.top", {"start": v(-245.68, -338.45) * mm, "end": v(-207.58, -338.45) * mm});
            skLineSegment(sketch, "E161.left", {"start": v(-258.38, 194.95) * mm, "end": v(-258.38, 17.15) * mm});
            skLineSegment(sketch, "E162.top", {"start": v(-182.18, -313.05) * mm, "end": v(109.92, -313.05) * mm});
            skLineSegment(sketch, "E162.left", {"start": v(-207.58, -338.45) * mm, "end": v(-207.58, -338.45) * mm});
            skLineSegment(sketch, "E162.right", {"start": v(135.32, -338.45) * mm, "end": v(135.32, -338.45) * mm});
            skLineSegment(sketch, "E163.trimOffspring", {"start": v(135.32, -338.45) * mm, "end": v(173.42, -338.45) * mm});
            skPoint(sketch, "E164.visualSharp", {"position": v(-207.58, -313.05) * mm});
            skArc(sketch, "E164.filletArc", {"start": v(-182.18, -313.05) * mm, "mid": v(-200.15, -320.49) * mm, "end": v(-207.58, -338.45) * mm});
            skPoint(sketch, "E165.visualSharp", {"position": v(135.32, -313.05) * mm});
            skArc(sketch, "E165.filletArc", {"start": v(135.32, -338.45) * mm, "mid": v(127.88, -320.49) * mm, "end": v(109.92, -313.05) * mm});
            skLineSegment(sketch, "E166.top", {"start": v(-245.68, 258.45) * mm, "end": v(-169.48, 258.45) * mm});
            skLineSegment(sketch, "E166.right", {"start": v(-169.48, 271.15) * mm, "end": v(-169.48, 258.45) * mm});
            skLineSegment(sketch, "E167.top", {"start": v(-80.58, 258.45) * mm, "end": v(8.32, 258.45) * mm});
            skLineSegment(sketch, "E167.left", {"start": v(-80.58, 271.15) * mm, "end": v(-80.58, 258.45) * mm});
            skLineSegment(sketch, "E167.right", {"start": v(8.32, 271.15) * mm, "end": v(8.32, 258.45) * mm});
            skLineSegment(sketch, "E168.top", {"start": v(173.42, 258.45) * mm, "end": v(97.22, 258.45) * mm});
            skLineSegment(sketch, "E168.right", {"start": v(97.22, 271.15) * mm, "end": v(97.22, 258.45) * mm});
            skLineSegment(sketch, "E169.top", {"start": v(186.12, 169.55) * mm, "end": v(173.42, 169.55) * mm});
            skLineSegment(sketch, "E170.bottom", {"start": v(186.12, 67.95) * mm, "end": v(173.42, 67.95) * mm});
            skLineSegment(sketch, "E170.top", {"start": v(186.12, -33.65) * mm, "end": v(173.42, -33.65) * mm});
            skLineSegment(sketch, "E171.bottom", {"start": v(186.12, -135.25) * mm, "end": v(173.42, -135.25) * mm});
            skLineSegment(sketch, "E171.top", {"start": v(186.12, -236.85) * mm, "end": v(173.42, -236.85) * mm});
            skLineSegment(sketch, "E172.bottom", {"start": v(-169.48, 17.15) * mm, "end": v(-80.58, 17.15) * mm});
            skLineSegment(sketch, "E172.top", {"start": v(-169.48, 4.45) * mm, "end": v(-80.58, 4.45) * mm});
            skLineSegment(sketch, "E172.left", {"start": v(-169.48, 17.15) * mm, "end": v(-169.48, 4.45) * mm});
            skLineSegment(sketch, "E172.right", {"start": v(-80.58, 17.15) * mm, "end": v(-80.58, 4.45) * mm});
            skLineSegment(sketch, "E173.bottom", {"start": v(8.32, 17.15) * mm, "end": v(97.22, 17.15) * mm});
            skLineSegment(sketch, "E173.top", {"start": v(8.32, 4.45) * mm, "end": v(97.22, 4.45) * mm});
            skLineSegment(sketch, "E173.left", {"start": v(8.32, 17.15) * mm, "end": v(8.32, 4.45) * mm});
            skLineSegment(sketch, "E173.right", {"start": v(97.22, 17.15) * mm, "end": v(97.22, 4.45) * mm});
            skLineSegment(sketch, "E174.bottom", {"start": v(-169.48, -236.85) * mm, "end": v(-80.58, -236.85) * mm});
            skLineSegment(sketch, "E174.top", {"start": v(-169.48, -249.55) * mm, "end": v(-80.58, -249.55) * mm});
            skLineSegment(sketch, "E174.left", {"start": v(-169.48, -236.85) * mm, "end": v(-169.48, -249.55) * mm});
            skLineSegment(sketch, "E174.right", {"start": v(-80.58, -236.85) * mm, "end": v(-80.58, -249.55) * mm});
            skLineSegment(sketch, "E175.bottom", {"start": v(8.32, -236.85) * mm, "end": v(97.22, -236.85) * mm});
            skLineSegment(sketch, "E175.top", {"start": v(8.32, -249.55) * mm, "end": v(97.22, -249.55) * mm});
            skLineSegment(sketch, "E175.left", {"start": v(8.32, -236.85) * mm, "end": v(8.32, -249.55) * mm});
            skLineSegment(sketch, "E175.right", {"start": v(97.22, -236.85) * mm, "end": v(97.22, -249.55) * mm});
            skLineSegment(sketch, "E176.bottom", {"start": v(-80.58, 220.35) * mm, "end": v(8.32, 220.35) * mm});
            skLineSegment(sketch, "E176.top", {"start": v(-80.58, 182.25) * mm, "end": v(8.32, 182.25) * mm});
            skLineSegment(sketch, "E176.left", {"start": v(-93.28, 207.65) * mm, "end": v(-93.28, 194.95) * mm});
            skLineSegment(sketch, "E176.right", {"start": v(21.02, 207.65) * mm, "end": v(21.02, 194.95) * mm});
            skLineSegment(sketch, "E177.top", {"start": v(-258.38, 194.95) * mm, "end": v(-245.68, 194.95) * mm});
            skLineSegment(sketch, "E177.right", {"start": v(-245.68, 258.45) * mm, "end": v(-245.68, 194.95) * mm});
            skLineSegment(sketch, "E178.bottom", {"start": v(-258.38, 17.15) * mm, "end": v(-245.68, 17.15) * mm});
            skLineSegment(sketch, "E178.top", {"start": v(-258.38, -59.05) * mm, "end": v(-245.68, -59.05) * mm});
            skLineSegment(sketch, "E178.right", {"start": v(-245.68, 17.15) * mm, "end": v(-245.68, -59.05) * mm});
            skLineSegment(sketch, "E179.top", {"start": v(-258.38, -236.85) * mm, "end": v(-245.68, -236.85) * mm});
            skLineSegment(sketch, "E179.right", {"start": v(-245.68, -338.45) * mm, "end": v(-245.68, -236.85) * mm});
            skPoint(sketch, "E177.bottom.start.orphan", {"position": v(-258.38, 271.15) * mm});
            skPoint(sketch, "E180.orphan", {"position": v(-245.68, 271.15) * mm});
            skLineSegment(sketch, "E181.trimOffspring", {"start": v(8.32, 271.15) * mm, "end": v(97.22, 271.15) * mm});
            skPoint(sketch, "E182.trimOffspring.end.orphan", {"position": v(186.12, 271.15) * mm});
            skPoint(sketch, "E183.orphan", {"position": v(186.12, 258.45) * mm});
            skPoint(sketch, "E184.orphan", {"position": v(173.42, 271.15) * mm});
            skLineSegment(sketch, "E185.trimOffspring", {"start": v(-258.38, -59.05) * mm, "end": v(-258.38, -236.85) * mm});
            skPoint(sketch, "E186.orphan", {"position": v(-258.38, -338.45) * mm});
            skPoint(sketch, "E187.visualSharp", {"position": v(21.02, 220.35) * mm});
            skArc(sketch, "E187.filletArc", {"start": v(21.02, 207.65) * mm, "mid": v(17.3, 216.63) * mm, "end": v(8.32, 220.35) * mm});
            skPoint(sketch, "E188.visualSharp", {"position": v(21.02, 182.25) * mm});
            skArc(sketch, "E188.filletArc", {"start": v(8.32, 182.25) * mm, "mid": v(17.3, 185.97) * mm, "end": v(21.02, 194.95) * mm});
            skPoint(sketch, "E189.visualSharp", {"position": v(-93.28, 182.25) * mm});
            skArc(sketch, "E189.filletArc", {"start": v(-93.28, 194.95) * mm, "mid": v(-89.56, 185.97) * mm, "end": v(-80.58, 182.25) * mm});
            skPoint(sketch, "E190.visualSharp", {"position": v(-93.28, 220.35) * mm});
            skArc(sketch, "E190.filletArc", {"start": v(-80.58, 220.35) * mm, "mid": v(-89.56, 216.63) * mm, "end": v(-93.28, 207.65) * mm});
            skLineSegment(sketch, "E191.bottom", {"start": v(173.42, 258.45) * mm, "end": v(186.12, 258.45) * mm});
            skLineSegment(sketch, "E191.top", {"start": v(173.42, 169.55) * mm, "end": v(186.12, 169.55) * mm});
            skLineSegment(sketch, "E191.right", {"start": v(186.12, 258.45) * mm, "end": v(186.12, 169.55) * mm});
            skLineSegment(sketch, "E192.bottom", {"start": v(173.42, 67.95) * mm, "end": v(186.12, 67.95) * mm});
            skLineSegment(sketch, "E192.top", {"start": v(173.42, -33.65) * mm, "end": v(186.12, -33.65) * mm});
            skLineSegment(sketch, "E192.right", {"start": v(186.12, 67.95) * mm, "end": v(186.12, -33.65) * mm});
            skLineSegment(sketch, "E193.bottom", {"start": v(173.42, -135.25) * mm, "end": v(186.12, -135.25) * mm});
            skLineSegment(sketch, "E193.top", {"start": v(173.42, -236.85) * mm, "end": v(186.12, -236.85) * mm});
            skLineSegment(sketch, "E193.right", {"start": v(186.12, -135.25) * mm, "end": v(186.12, -236.85) * mm});
            skLineSegment(sketch, "E194.left", {"start": v(173.42, 169.55) * mm, "end": v(173.42, 67.95) * mm});
            skLineSegment(sketch, "E195.left", {"start": v(173.42, -33.65) * mm, "end": v(173.42, -135.25) * mm});
            skLineSegment(sketch, "E196.left", {"start": v(173.42, -236.85) * mm, "end": v(173.42, -338.45) * mm});
            skPoint(sketch, "E196.top.end.orphan", {"position": v(186.12, -338.45) * mm});
            skSolve(sketch);
        }
        {
            var Q0;
            Q0 = qSketchRegion(id + "F14", true);
            extrude(context, id + "F15", {"entities" : qUnion([Q0]), "depth" : 12.7 * mm});
        }
        {
            var Q0;
            Q0=qCreatedBy(makeId("Top.planeOp"),FACE);
            var sketch = newSketch(context, id + "F16", { "sketchPlane" : qUnion([Q0])});
            skLineSegment(sketch, "E197.bottom", {"start": v(-498.13, -347.6) * mm, "end": v(-447.33, -347.6) * mm});
            skLineSegment(sketch, "E197.top", {"start": v(-383.83, 262) * mm, "end": v(-288.58, 262) * mm});
            skLineSegment(sketch, "E197.left", {"start": v(-498.13, -347.6) * mm, "end": v(-498.13, -246) * mm});
            skLineSegment(sketch, "E197.right", {"start": v(454.37, -347.7) * mm, "end": v(454.37, -246.1) * mm});
            skLineSegment(sketch, "E198.top", {"start": v(-485.43, 249.3) * mm, "end": v(-383.26, 249.3) * mm});
            skLineSegment(sketch, "E198.right", {"start": v(-383.83, 262) * mm, "end": v(-383.26, 249.3) * mm});
            skLineSegment(sketch, "E199.top", {"start": v(-288.58, 249.2) * mm, "end": v(-174.28, 249.2) * mm});
            skLineSegment(sketch, "E199.left", {"start": v(-288.58, 262) * mm, "end": v(-288.58, 249.2) * mm});
            skLineSegment(sketch, "E199.right", {"start": v(-174.28, 262) * mm, "end": v(-174.28, 249.2) * mm});
            skLineSegment(sketch, "E200.top", {"start": v(-79.03, 249.2) * mm, "end": v(35.27, 249.2) * mm});
            skLineSegment(sketch, "E200.left", {"start": v(-79.03, 262) * mm, "end": v(-79.03, 249.2) * mm});
            skLineSegment(sketch, "E200.right", {"start": v(35.27, 262) * mm, "end": v(35.27, 249.2) * mm});
            skLineSegment(sketch, "E201.top", {"start": v(130.52, 249.2) * mm, "end": v(244.82, 249.2) * mm});
            skLineSegment(sketch, "E201.left", {"start": v(130.52, 262) * mm, "end": v(130.52, 249.2) * mm});
            skLineSegment(sketch, "E201.right", {"start": v(244.82, 262) * mm, "end": v(244.82, 249.2) * mm});
            skLineSegment(sketch, "E202.top", {"start": v(340.07, 249.3) * mm, "end": v(441.67, 249.3) * mm});
            skLineSegment(sketch, "E202.left", {"start": v(340.07, 262) * mm, "end": v(340.07, 249.3) * mm});
            skLineSegment(sketch, "E203.trimOffspring", {"start": v(-174.28, 262) * mm, "end": v(-79.03, 262) * mm});
            skLineSegment(sketch, "E204.trimOffspring", {"start": v(35.27, 262) * mm, "end": v(130.52, 262) * mm});
            skLineSegment(sketch, "E205.trimOffspring", {"start": v(244.82, 262) * mm, "end": v(340.07, 262) * mm});
            skLineSegment(sketch, "E206.top", {"start": v(-421.93, -322.2) * mm, "end": v(378.17, -322.2) * mm});
            skLineSegment(sketch, "E206.left", {"start": v(-447.33, -347.6) * mm, "end": v(-447.33, -347.6) * mm});
            skPoint(sketch, "E207.visualSharp", {"position": v(-447.33, -322.2) * mm});
            skArc(sketch, "E207.filletArc", {"start": v(-421.93, -322.2) * mm, "mid": v(-439.89, -329.63) * mm, "end": v(-447.33, -347.6) * mm});
            skPoint(sketch, "E208.visualSharp", {"position": v(403.57, -322.2) * mm});
            skArc(sketch, "E208.filletArc", {"start": v(403.57, -347.7) * mm, "mid": v(396.17, -329.67) * mm, "end": v(378.17, -322.2) * mm});
            skLineSegment(sketch, "E209.trimOffspring", {"start": v(403.57, -347.7) * mm, "end": v(454.37, -347.7) * mm});
            skLineSegment(sketch, "E210.top", {"start": v(454.37, 160.3) * mm, "end": v(441.67, 160.3) * mm});
            skLineSegment(sketch, "E210.right", {"start": v(441.67, 249.3) * mm, "end": v(441.67, 160.3) * mm});
            skLineSegment(sketch, "E211.bottom", {"start": v(454.37, 58.7) * mm, "end": v(441.67, 58.7) * mm});
            skLineSegment(sketch, "E211.top", {"start": v(454.37, -42.9) * mm, "end": v(441.67, -42.9) * mm});
            skLineSegment(sketch, "E211.right", {"start": v(441.67, 58.7) * mm, "end": v(441.67, -42.9) * mm});
            skLineSegment(sketch, "E212.bottom", {"start": v(454.37, -144.5) * mm, "end": v(441.67, -144.5) * mm});
            skLineSegment(sketch, "E212.top", {"start": v(454.37, -246.1) * mm, "end": v(441.67, -246.1) * mm});
            skLineSegment(sketch, "E212.right", {"start": v(441.67, -144.5) * mm, "end": v(441.67, -246.1) * mm});
            skLineSegment(sketch, "E213.top", {"start": v(-498.13, 160.4) * mm, "end": v(-485.43, 160.4) * mm});
            skLineSegment(sketch, "E213.right", {"start": v(-485.43, 249.3) * mm, "end": v(-485.43, 160.4) * mm});
            skPoint(sketch, "E214.oppositeSnap0", {"position": v(-498.13, -42.8) * mm});
            skLineSegment(sketch, "E214.bottom", {"start": v(-498.13, 58.8) * mm, "end": v(-485.43, 58.8) * mm});
            skLineSegment(sketch, "E214.top", {"start": v(-498.13, -42.8) * mm, "end": v(-485.43, -42.8) * mm});
            skLineSegment(sketch, "E214.right", {"start": v(-485.43, 58.8) * mm, "end": v(-485.43, -42.8) * mm});
            skLineSegment(sketch, "E215.bottom", {"start": v(-498.13, -144.4) * mm, "end": v(-485.43, -144.4) * mm});
            skLineSegment(sketch, "E215.top", {"start": v(-498.13, -246) * mm, "end": v(-485.43, -246) * mm});
            skLineSegment(sketch, "E215.right", {"start": v(-485.43, -144.4) * mm, "end": v(-485.43, -246) * mm});
            skPoint(sketch, "E216.trimOffspring.start.orphan", {"position": v(441.67, 261.9) * mm});
            skPoint(sketch, "E202.right.start.orphan", {"position": v(454.37, 261.9) * mm});
            skLineSegment(sketch, "E217.trimOffspring", {"start": v(454.37, 58.7) * mm, "end": v(454.37, 160.3) * mm});
            skLineSegment(sketch, "E218.trimOffspring", {"start": v(454.37, -144.5) * mm, "end": v(454.37, -42.9) * mm});
            skLineSegment(sketch, "E219.trimOffspring", {"start": v(-498.13, 58.8) * mm, "end": v(-498.13, 160.4) * mm});
            skLineSegment(sketch, "E220.trimOffspring", {"start": v(-498.13, -144.4) * mm, "end": v(-498.13, -42.8) * mm});
            skPoint(sketch, "E221.orphan", {"position": v(-498.13, 262) * mm});
            skPoint(sketch, "E222.orphan", {"position": v(-485.43, 262) * mm});
            skPoint(sketch, "E223.orphan", {"position": v(-498.13, 249.3) * mm});
            skLineSegment(sketch, "E224.bottom", {"start": v(-383.83, 8) * mm, "end": v(-288.58, 8) * mm});
            skLineSegment(sketch, "E224.top", {"start": v(-383.83, -4.7) * mm, "end": v(-288.58, -4.7) * mm});
            skLineSegment(sketch, "E224.left", {"start": v(-383.83, 8) * mm, "end": v(-383.83, -4.7) * mm});
            skLineSegment(sketch, "E224.right", {"start": v(-288.58, 8) * mm, "end": v(-288.58, -4.7) * mm});
            skLineSegment(sketch, "E225.bottom", {"start": v(-174.28, 8) * mm, "end": v(-79.03, 8) * mm});
            skLineSegment(sketch, "E225.top", {"start": v(-174.28, -4.31) * mm, "end": v(-79.03, -4.31) * mm});
            skLineSegment(sketch, "E225.left", {"start": v(-174.28, 8) * mm, "end": v(-174.28, -4.31) * mm});
            skLineSegment(sketch, "E225.right", {"start": v(-79.03, 8) * mm, "end": v(-79.03, -4.31) * mm});
            skLineSegment(sketch, "E226.bottom", {"start": v(35.27, 8) * mm, "end": v(130.52, 8) * mm});
            skLineSegment(sketch, "E226.top", {"start": v(35.27, -4.7) * mm, "end": v(130.52, -4.7) * mm});
            skLineSegment(sketch, "E226.left", {"start": v(35.27, 8) * mm, "end": v(35.27, -4.7) * mm});
            skLineSegment(sketch, "E226.right", {"start": v(130.52, 8) * mm, "end": v(130.52, -4.7) * mm});
            skLineSegment(sketch, "E227.bottom", {"start": v(244.82, 8) * mm, "end": v(340.07, 8) * mm});
            skLineSegment(sketch, "E227.top", {"start": v(244.82, -4.7) * mm, "end": v(340.07, -4.7) * mm});
            skLineSegment(sketch, "E227.left", {"start": v(244.82, 8) * mm, "end": v(244.82, -4.7) * mm});
            skLineSegment(sketch, "E227.right", {"start": v(340.07, 8) * mm, "end": v(340.07, -4.7) * mm});
            skLineSegment(sketch, "E228.bottom", {"start": v(-383.83, -246) * mm, "end": v(-288.58, -246) * mm});
            skLineSegment(sketch, "E228.top", {"start": v(-383.83, -258.7) * mm, "end": v(-288.58, -258.7) * mm});
            skLineSegment(sketch, "E228.left", {"start": v(-383.83, -246) * mm, "end": v(-383.83, -258.7) * mm});
            skLineSegment(sketch, "E228.right", {"start": v(-288.58, -246) * mm, "end": v(-288.58, -258.7) * mm});
            skLineSegment(sketch, "E229.bottom", {"start": v(-174.28, -246) * mm, "end": v(-79.03, -246) * mm});
            skLineSegment(sketch, "E229.top", {"start": v(-174.28, -258.7) * mm, "end": v(-79.03, -258.7) * mm});
            skLineSegment(sketch, "E229.left", {"start": v(-174.28, -246) * mm, "end": v(-174.28, -258.7) * mm});
            skLineSegment(sketch, "E229.right", {"start": v(-79.03, -246) * mm, "end": v(-79.03, -258.7) * mm});
            skPoint(sketch, "E230.oppositeSnap0", {"position": v(-126.65, -258.7) * mm});
            skLineSegment(sketch, "E230.bottom", {"start": v(35.27, -246) * mm, "end": v(130.52, -246) * mm});
            skLineSegment(sketch, "E230.top", {"start": v(35.27, -258.7) * mm, "end": v(130.52, -258.7) * mm});
            skLineSegment(sketch, "E230.left", {"start": v(35.27, -246) * mm, "end": v(35.27, -258.7) * mm});
            skLineSegment(sketch, "E230.right", {"start": v(130.52, -246) * mm, "end": v(130.52, -258.7) * mm});
            skLineSegment(sketch, "E231.bottom", {"start": v(244.82, -246) * mm, "end": v(340.07, -246) * mm});
            skLineSegment(sketch, "E231.top", {"start": v(244.82, -258.7) * mm, "end": v(340.07, -258.7) * mm});
            skLineSegment(sketch, "E231.left", {"start": v(244.82, -246) * mm, "end": v(244.82, -258.7) * mm});
            skLineSegment(sketch, "E231.right", {"start": v(340.07, -246) * mm, "end": v(340.07, -258.7) * mm});
            skPoint(sketch, "E206.right.start.orphan", {"position": v(403.57, -335) * mm});
            skSolve(sketch);
        }
        {
            var Q0;
            Q0 = qSketchRegion(id + "F16", true);
            extrude(context, id + "F17", {"entities" : qUnion([Q0]), "depth" : 12.7 * mm});
        }
        {
            var Q0;
            Q0=qCreatedBy(makeId("Front.planeOp"),FACE);
            var sketch = newSketch(context, id + "F18", { "sketchPlane" : qUnion([Q0])});
            skLineSegment(sketch, "E232.bottom", {"start": v(-242.23, 384.76) * mm, "end": v(225.13, 384.76) * mm});
            skLineSegment(sketch, "E232.top", {"start": v(-242.23, -97.84) * mm, "end": v(225.13, -97.84) * mm});
            skLineSegment(sketch, "E232.left", {"start": v(-242.23, 384.76) * mm, "end": v(-242.23, -97.84) * mm});
            skLineSegment(sketch, "E232.right", {"start": v(225.13, 384.76) * mm, "end": v(225.13, -97.84) * mm});
            skLineSegment(sketch, "E233.bottom", {"start": v(225.13, 384.76) * mm, "end": v(240.37, 384.76) * mm});
            skLineSegment(sketch, "E233.top", {"start": v(225.13, -97.84) * mm, "end": v(240.37, -97.84) * mm});
            skLineSegment(sketch, "E233.right", {"start": v(240.37, 384.76) * mm, "end": v(240.37, -97.84) * mm});
            skSolve(sketch);
        }
        {
            var Q0;
            Q0=makeQuery(id+"F18.imprint","IMPRINT",FACE,{"disambiguationData":[TD([[makeQuery(id+"F18.imprint","IMPRINT",EDGE,{"derivedFrom":sQuery(id+"F18.wireOp",EDGE,"E232.bottom")}),-1.0]])]});
            extrude(context, id + "F19", {"entities" : qUnion([Q0]), "depth" : 12.7 * mm});
        }
        {
            var Q0;
            Q0=makeQuery(id+"F18.imprint","IMPRINT",FACE,{"disambiguationData":[TD([[makeQuery(id+"F18.imprint","IMPRINT",EDGE,{"derivedFrom":sQuery(id+"F18.wireOp",EDGE,"E233.bottom")}),-1.0]])]});
            extrude(context, id + "F20", {"entities" : qUnion([Q0]), "operationType" : NewBodyOperationType.ADD, "depth" : 6.35 * mm});
        }
        {
            var Q0;
            Q0=qCreatedBy(makeId("Front.planeOp"),FACE);
            var sketch = newSketch(context, id + "F21", { "sketchPlane" : qUnion([Q0])});
            skLineSegment(sketch, "E234.bottom", {"start": v(-501.7, 62.55) * mm, "end": v(476.2, 62.55) * mm});
            skLineSegment(sketch, "E234.top", {"start": v(-501.7, 14.3) * mm, "end": v(476.2, 14.3) * mm});
            skLineSegment(sketch, "E234.left", {"start": v(-501.7, 62.55) * mm, "end": v(-501.7, 14.3) * mm});
            skLineSegment(sketch, "E234.right", {"start": v(476.2, 62.55) * mm, "end": v(476.2, 14.3) * mm});
            skSolve(sketch);
        }
        {
            var Q0;
            Q0 = qSketchRegion(id + "F21", true);
            extrude(context, id + "F22", {"entities" : qUnion([Q0]), "depth" : 12.7 * mm});
        }
        {
            var Q0;
            Q0=qCreatedBy(makeId("Front.planeOp"),FACE);
            var sketch = newSketch(context, id + "F23", { "sketchPlane" : qUnion([Q0])});
            skLineSegment(sketch, "E235.bottom", {"start": v(-171.23, 105.4) * mm, "end": v(273.27, 105.4) * mm});
            skLineSegment(sketch, "E235.top", {"start": v(-171.23, 57.15) * mm, "end": v(273.27, 57.15) * mm});
            skLineSegment(sketch, "E235.left", {"start": v(-171.23, 105.4) * mm, "end": v(-171.23, 57.15) * mm});
            skLineSegment(sketch, "E235.right", {"start": v(273.27, 105.4) * mm, "end": v(273.27, 57.15) * mm});
            skSolve(sketch);
        }
        {
            var Q0;
            Q0 = qSketchRegion(id + "F23", true);
            extrude(context, id + "F24", {"entities" : qUnion([Q0]), "depth" : 12.7 * mm});
        }
    });
